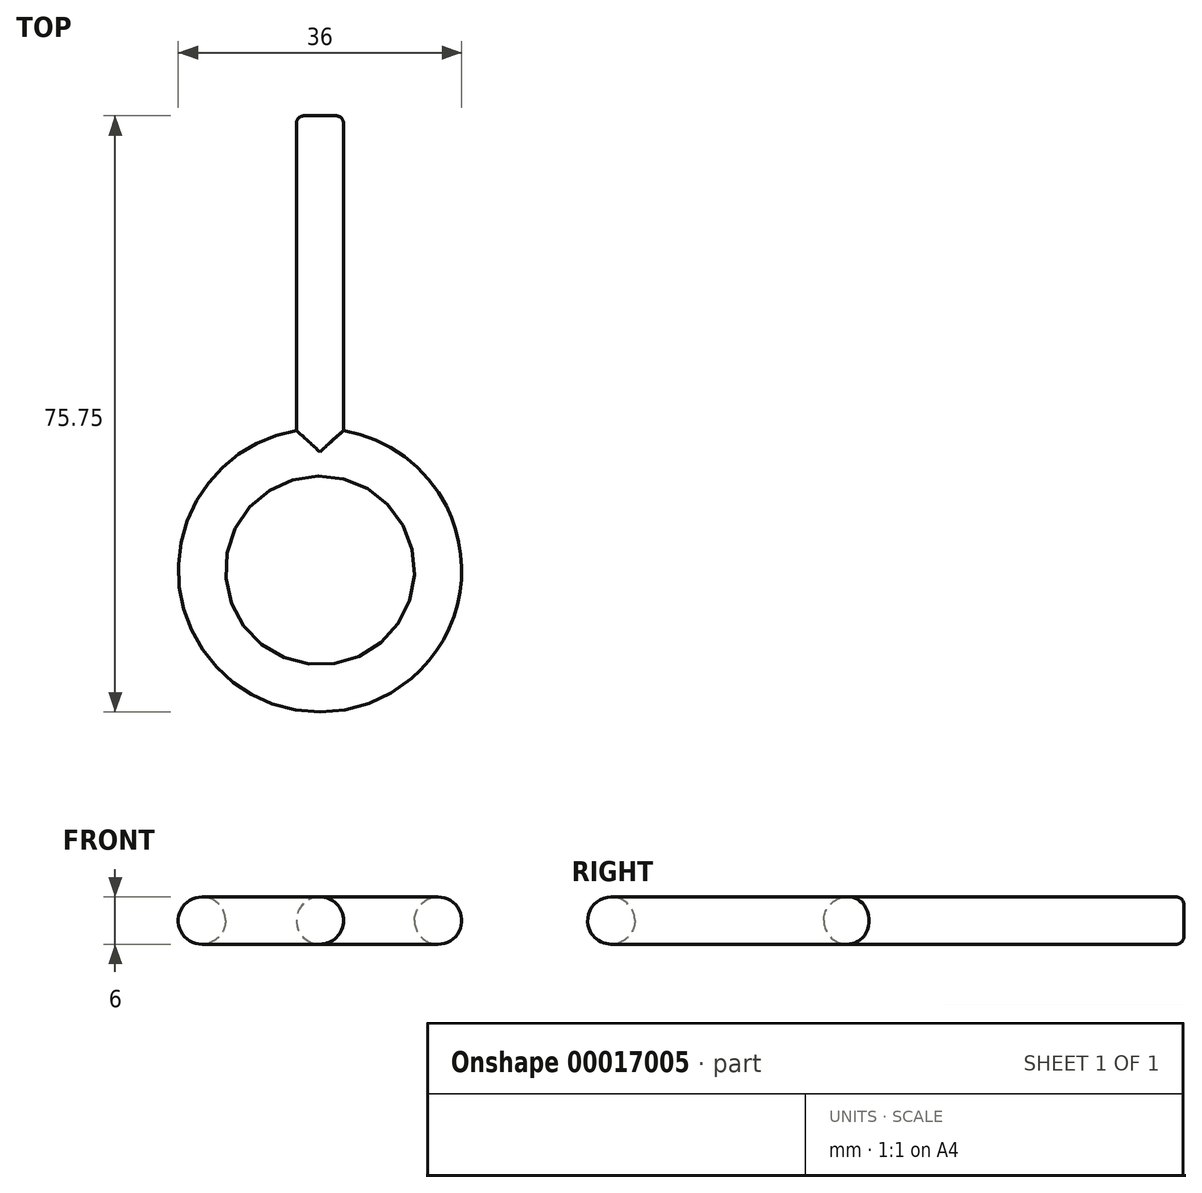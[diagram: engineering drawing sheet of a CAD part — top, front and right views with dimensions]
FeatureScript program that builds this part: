
annotation { "Feature Type Name" : "Feature", "Feature Type Description" : "" }
export const myFeature = defineFeature(function(context is Context, id is Id, definition is map)
    precondition{}
    {
        {
            var Q0;
            Q0=qCreatedBy(makeId("Front.planeOp"),FACE);
            var sketch = newSketch(context, id + "F0", { "sketchPlane" : qUnion([Q0])});
            skCircle(sketch, "E0", {"center": v(0, 0) * mm, "radius": 3 * mm});
            skSolve(sketch);
        }
        {
            var Q0;
            Q0 = qSketchRegion(id + "F0", true);
            extrude(context, id + "F1", {"entities" : qUnion([Q0]), "oppositeDirection" : true, "depth" : 42.75 * mm});
        }
        {
            var Q0;
            Q0=qCreatedBy(makeId("Front.planeOp"),FACE);
            cPlane(context, id + "F2", {"entities" : qUnion([Q0]), "cplaneType" : CPlaneType.OFFSET, "offset" : 15 * mm, "width" : 150 * mm, "height" : 150 * mm});
        }
        {
            var Q0;
            Q0=qCreatedBy(id+"F2.planeOp",FACE);
            var sketch = newSketch(context, id + "F3", { "sketchPlane" : qUnion([Q0])});
            skCircle(sketch, "E1", {"center": v(15, 0) * mm, "radius": 3 * mm});
            skLineSegment(sketch, "E2", {"start": v(0, 0) * mm, "end": v(0, 10) * mm});
            skSolve(sketch);
        }
        {
            var Q0;
            Q0=makeQuery(id+"F3.imprint","IMPRINT",FACE,{"disambiguationData":[TD([[makeQuery(id+"F3.imprint","IMPRINT",EDGE,{"derivedFrom":sQuery(id+"F3.wireOp",EDGE,"E1")}),1.0]])]});
            var Q1;
            Q1=sQuery(id+"F3.wireOp",EDGE,"E1");
            var Q2;
            Q2=sQuery(id+"F3.wireOp",EDGE,"E2");
            revolve(context, id + "F4", {"operationType" : NewBodyOperationType.ADD, "entities" : qUnion([Q0]), "surfaceEntities" : qUnion([Q1]), "axis" : qUnion([Q2]), "revolveType" : RevolveType.FULL});
        }
        {
            var Q0;
            Q0=makeQuery(id+"F1.opExtrude","CAP_EDGE",EDGE,{"disambiguationData":[OSD([sQuery(id+"F0.wireOp",EDGE,"E0")])],"isStart":false});
            fillet(context, id + "F5", {"entities" : qUnion([Q0]), "radius" : 1 * mm, "tangentPropagation" : true, "allowEdgeOverflow" : false});
        }
    });
